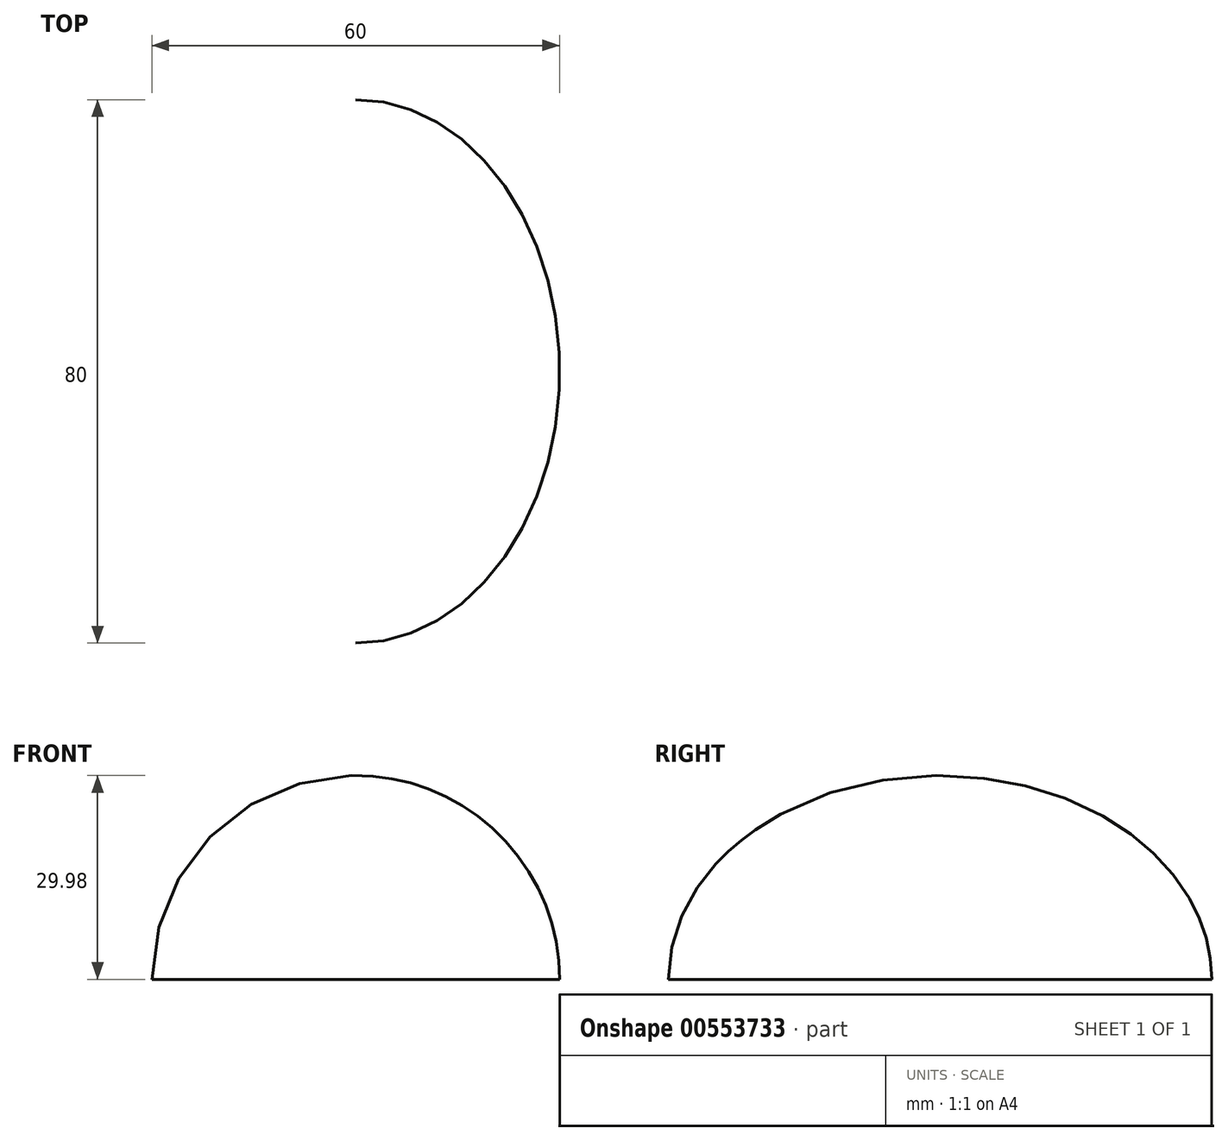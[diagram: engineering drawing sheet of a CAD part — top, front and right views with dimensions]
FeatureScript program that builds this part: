
annotation { "Feature Type Name" : "Feature", "Feature Type Description" : "" }
export const myFeature = defineFeature(function(context is Context, id is Id, definition is map)
    precondition{}
    {
        {
            var Q0;
            Q0=qCreatedBy(makeId("Top.planeOp"),FACE);
            var sketch = newSketch(context, id + "F0", { "sketchPlane" : qUnion([Q0])});
            skEllipse(sketch, "E0", {"center": v(0, 0) * mm, "majorRadius": 40 * mm, "minorRadius": 30 * mm, "majorAxis": v(0, 1)});
            skLineSegment(sketch, "E1", {"start": v(0, -40) * mm, "end": v(0, 40) * mm});
            skSolve(sketch);
        }
        {
            var Q0;
            {var subQ0=sQuery(id+"F0.wireOp",EDGE,"E1");Q0=makeQuery(id+"F0.imprint","IMPRINT",FACE,{"disambiguationData":[TD([[makeQuery(id+"F0.imprint","IMPRINT",EDGE,{"derivedFrom":subQ0}),1.0]])]});}
            var Q1;
            Q1=sQuery(id+"F0.wireOp",EDGE,"E1");
            revolve(context, id + "F1", {"entities" : qUnion([Q0]), "axis" : qUnion([Q1]), "revolveType" : RevolveType.ONE_DIRECTION, "angle" : 180 * degree});
        }
    });
